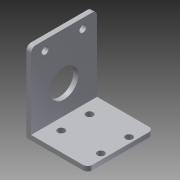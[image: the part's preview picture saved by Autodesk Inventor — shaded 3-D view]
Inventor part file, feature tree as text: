
AUTODESK INVENTOR PART (.ipt)
format: ipt  version: 2013 (Build 170138000, 138)  size: 135,680 bytes
history: native  units: in
note: dims shown in document units (in); Inventor stores cm internally (conversion verified against a paired STEP export)
features: extrude x3, sketch x3, fillet x1
ambient origin geometry x8: Origin, YZ Plane, XZ Plane, XY Plane, X Axis, Y Axis, Z Axis, Center Point
bodies: Solid1 (feature_tree)
feature tree (7):
  extrude  "Extrusion1"  Depth=2.5in
  extrude  "Extrusion2"  Depth=1.75in TaperAngle=0.0deg
  extrude  "Extrusion3"  Depth=0.625in
  fillet  "Fillet1"  Radius=0.1875in
  sketch  "Sketch1"  dims[d0=2.0in d1=2.5in]
  sketch  "Sketch2"  dims[d2=0.125in d3=1.75in d4=0.0in]
  sketch  "Sketch3"  dims[d5=1.0in d6=0.625in d7=0.1875in d8=0.1875in d9=1.5in d10=0.0in d11=0.75in d12=0.875in d13=0.75in d17=0.1875in d18=0.425in d19=1.0in d20=0.0in d21=1.625in d22=0.7874in d24=1.05in d25=0.3937in d27=1.0in d29=0.125in d30=0.375in]
